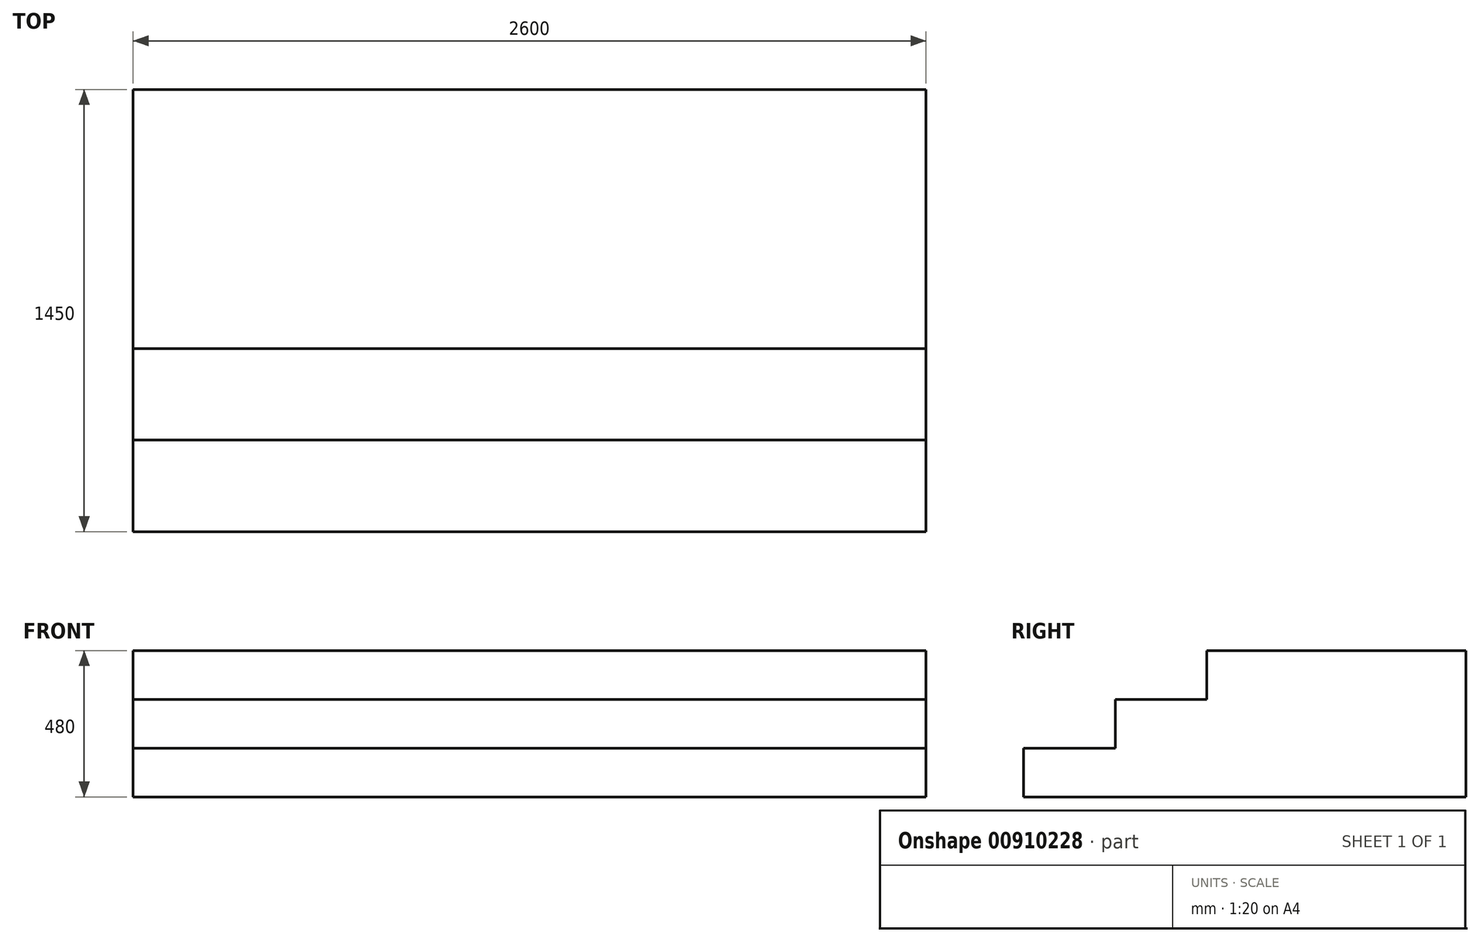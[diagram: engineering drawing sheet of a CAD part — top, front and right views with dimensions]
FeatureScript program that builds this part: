
annotation { "Feature Type Name" : "Feature", "Feature Type Description" : "" }
export const myFeature = defineFeature(function(context is Context, id is Id, definition is map)
    precondition{}
    {
        {
            var Q0;
            Q0=qCreatedBy(makeId("Right.planeOp"),FACE);
            var sketch = newSketch(context, id + "F0", { "sketchPlane" : qUnion([Q0])});
            skLineSegment(sketch, "E0", {"start": v(0, 0) * mm, "end": v(0, 160) * mm});
            skLineSegment(sketch, "E1", {"start": v(0, 160) * mm, "end": v(300, 160) * mm});
            skLineSegment(sketch, "E2", {"start": v(300, 160) * mm, "end": v(300, 320) * mm});
            skLineSegment(sketch, "E3", {"start": v(300, 320) * mm, "end": v(600, 320) * mm});
            skLineSegment(sketch, "E4", {"start": v(600, 320) * mm, "end": v(600, 480) * mm});
            skLineSegment(sketch, "E5", {"start": v(600, 480) * mm, "end": v(1450, 480) * mm});
            skLineSegment(sketch, "E6", {"start": v(1450, 480) * mm, "end": v(1450, 0) * mm});
            skLineSegment(sketch, "E7", {"start": v(1450, 0) * mm, "end": v(0, 0) * mm});
            skSolve(sketch);
        }
        {
            var Q0;
            Q0 = qSketchRegion(id + "F0", true);
            extrude(context, id + "F1", {"entities" : qUnion([Q0]), "endBound" : BoundingType.SYMMETRIC, "depth" : 2600 * mm, "offsetDistance" : 25 * mm});
        }
    });
